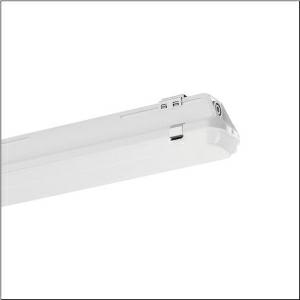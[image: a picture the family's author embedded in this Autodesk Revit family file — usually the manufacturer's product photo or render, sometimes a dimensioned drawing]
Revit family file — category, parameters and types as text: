
# Revit family: monsun_21_emergency_51fb107l447k3g
name_source: partatom
category: Lighting Fixtures
units: mm (PartAtom-declared; Revit-internal decimal feet)

## family parameters
Cut with Voids When Loaded = No
Host = Face
Light Source = No
Part Type = Normal
Room Calculation Point = No
Round Connector Dimension = Use Diameter
Shared = No

## types (1)
- --- (1 x LED, 4330 lm, 28.8 W, 4000K)
    Apparent Load = 29 VA
    CIE Flux Codes = 46 76 93 94 100
    Color Rendering = 80
    Color Temperature = 4000K
    Default Elevation = 1800 mm
    Description = Monsun 21 emergency, damp-proof luminaire, chain hanger, primary optical cover: enclosure, of PMMA, light emission: direct distribution, primary light characteristic: symmetric, installation type: suspended mounting, surface-mounted, horizontal mounting, vertical mounting, LED, rated luminous flux: 4.330lm, luminous efficacy: 173lm/W, light colour: 840, colour temperature: 4000K, control gear: ON/OFF, with terminal, 3-pole, max. 2.5mm², mains connection: 220..240V, AC, 50/60Hz, rated input power: 29W, control gear: single battery element, battery: LiFePO4, 9Ah, housing, of glass-fibre reinforced plastic, uncoated, bright grey, incl. chain hanger, length: 1.299mm, width: 90mm, height: 88mm, clip for enclosure, of stainless steel (V2A), ceiling mounting element, of stainless steel (V2A), chain hanger, of stainless steel (V2A), protection rating (complete): IP66, insulation class (complete): insulation class I (protective earthing), certification: CE, UKCA, protection symbol: D, impact resistance: IK04, permissible operating ambient temperature: +5..+25°C, standard: EN 50419, EN 60598-2-1, corresponds to IFS (International Featured Standards) requirements for safety and quality in the food industry, for indoor or canopied outdoor use, no direct snow, no direct sun, no direct rain, LABS conformity tested according to VDMA 24364:2018-05, contact your sales advisor before using the luminaires in applications with unclear chemical exposure, large temperature fluctuations or condensation-forming humidity, packaging unit: 1 piece
    Height = 88 mm
    Lamp = 1 x LED
    Lamp Light Flux = 4330 lm
    Lamp Power = 28.8 W
    Lamp count = 1
    Length = 1299 mm
    Luminous efficacy = 150 lm/W
    Manufacturer = Siteco
    ModVariant = No
    Model = 51FB107L447K3G
    Mounting Place = Ceiling
    Mounting Type = Surface mounted
    Number of Poles = 1
    OnlyDefault = Yes
    Power Factor = 1
    Product Name = Monsun 21 emergency
    Product group = damp-proof luminaire
    ProductGroupID = 300
    Protection Class = Protection class I
    Protection Degree = IP 66
    RLX_Detail_Level = 1
    RLX_Emergency_Light_Flux = 0 lm
    RLX_Emergency_Type = 0
    RLX_Emergency_Type_DB = No
    RlxData = <blob elided: 90029 chars, md5=8abb5b52>
    Socket = socket
    Standby Power = 0 W
    System Light Flux = 4330 lm
    System Power = 29 W
    Type Comments = -
    Type Image = l_1319656.jpg
    URL = http://relux.com
    VarID = @adj_037003
    Voltage = 0 V
    Weight = 0.00 kg
    Width = 90 mm

## geometry (parser evidence)
native form markers: Blend x4, Sweep x15
no freeform markers — native parametric forms only
